# Revit family: GN-100
name_source: partatom
category: Mechanical Equipment
units: mm (PartAtom-declared; Revit-internal decimal feet)

## family parameters
Always vertical = Yes
Cut with Voids When Loaded = No
Part Type = Normal
Room Calculation Point = No
Round Connector Dimension = Use Radius
Shared = No
Work Plane-Based = No

## types (6) — shared parameters
0 = 0' - 0"
1" = 0' - 1"
1.5 = 0' - 1 1/2"
15.5"/2 = 0' - 7 3/4"
2" = 0' - 2"
2' = 2' - 0"
3" = 0' - 3"
3.25" = 0' - 3 1/4"
4" = 0' - 4"
5.6875"/2 = 0' - 2 27/32"
5.9375"/2 = 0' - 2 31/32"
5/8 = 0' - 0 5/8"
6" = 0' - 6"
6.5" = 0' - 6 1/2"
6.6875"-3.25" = 0' - 3 7/16"
7" = 0' - 7"
8.375" = 0' - 8 3/8"
8.375"-(5.9375"/2) = 0' - 5 13/32"
A = 1' - 0 3/4"
A/2 = 0' - 6 3/8"
B = 1' - 2 3/4"
B/2 = 0' - 7 3/8"
Manufacturer = Loren Cook Company
ONE EIGTH = 0' - 0 1/8"
Type Comments = Inline Fans 100 Series
URL = www.lorencook.com

## per-type parameters (varying)
| type | Model |
| GNVF-180 | GNVF |
| GN-166/168 | GN |
| GN-146/148 | GN |
| GN-126/128 | GN |
| GNVF-100 | GNVF |
| GN-186/188 | GN |

## geometry (parser evidence)
native form markers: Sweep x2
no freeform markers — native parametric forms only
